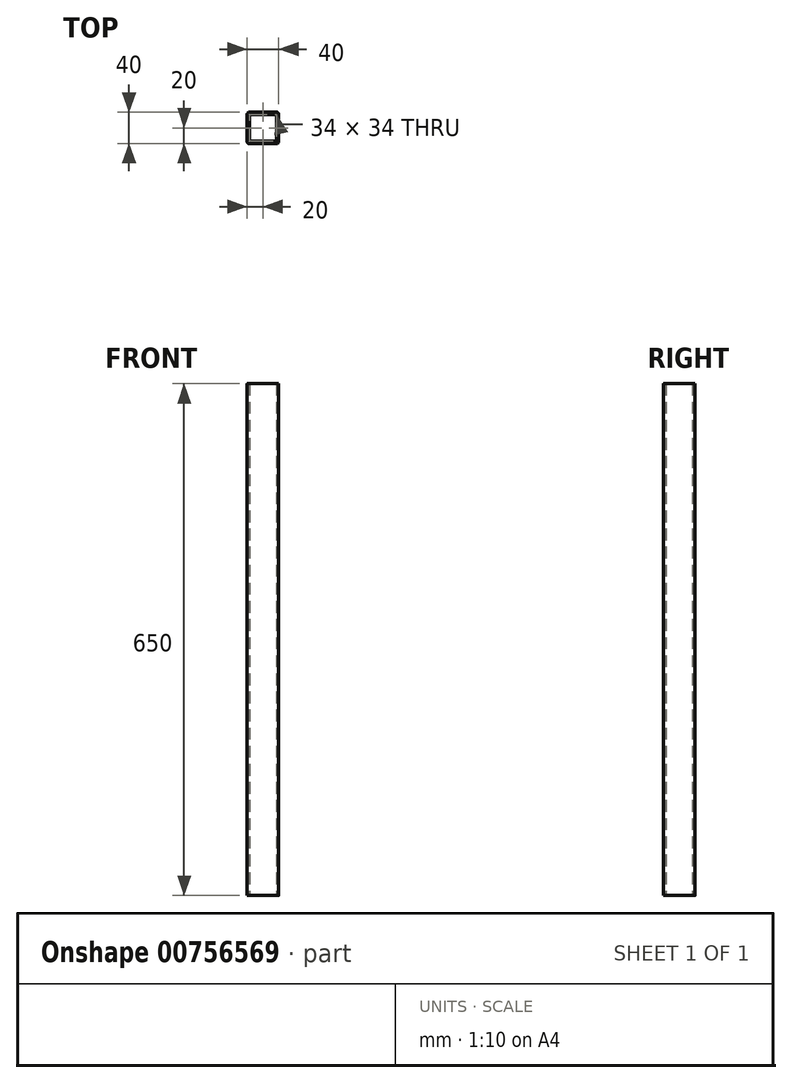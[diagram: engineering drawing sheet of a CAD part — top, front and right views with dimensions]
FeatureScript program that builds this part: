
annotation { "Feature Type Name" : "Feature", "Feature Type Description" : "" }
export const myFeature = defineFeature(function(context is Context, id is Id, definition is map)
    precondition{}
    {
        {
            var Q0;
            Q0=qCreatedBy(makeId("Top.planeOp"),FACE);
            var sketch = newSketch(context, id + "F0", { "sketchPlane" : qUnion([Q0])});
            skLineSegment(sketch, "E0.bottom", {"start": v(2.5, 0) * mm, "end": v(37.5, 0) * mm});
            skLineSegment(sketch, "E0.top", {"start": v(2.5, 40) * mm, "end": v(37.5, 40) * mm});
            skLineSegment(sketch, "E0.left", {"start": v(0, 2.5) * mm, "end": v(0, 37.5) * mm});
            skLineSegment(sketch, "E0.right", {"start": v(40, 2.5) * mm, "end": v(40, 37.5) * mm});
            skLineSegment(sketch, "E1.bottom", {"start": v(3, 3) * mm, "end": v(37, 3) * mm});
            skLineSegment(sketch, "E1.top", {"start": v(3, 37) * mm, "end": v(37, 37) * mm});
            skLineSegment(sketch, "E1.left", {"start": v(3, 3) * mm, "end": v(3, 37) * mm});
            skLineSegment(sketch, "E1.right", {"start": v(37, 3) * mm, "end": v(37, 37) * mm});
            skPoint(sketch, "E2.visualSharp", {"position": v(0, 0) * mm});
            skArc(sketch, "E2.filletArc", {"start": v(0, 2.5) * mm, "mid": v(0.73, 0.73) * mm, "end": v(2.5, 0) * mm});
            skPoint(sketch, "E3.visualSharp", {"position": v(40, 0) * mm});
            skArc(sketch, "E3.filletArc", {"start": v(37.5, 0) * mm, "mid": v(39.27, 0.73) * mm, "end": v(40, 2.5) * mm});
            skPoint(sketch, "E4.visualSharp", {"position": v(40, 40) * mm});
            skArc(sketch, "E4.filletArc", {"start": v(40, 37.5) * mm, "mid": v(39.27, 39.27) * mm, "end": v(37.5, 40) * mm});
            skPoint(sketch, "E5.visualSharp", {"position": v(0, 40) * mm});
            skArc(sketch, "E5.filletArc", {"start": v(2.5, 40) * mm, "mid": v(0.73, 39.27) * mm, "end": v(0, 37.5) * mm});
            skSolve(sketch);
        }
        {
            var Q0;
            Q0 = qSketchRegion(id + "F0", true);
            extrude(context, id + "F1", {"entities" : qUnion([Q0]), "depth" : 650 * mm, "offsetDistance" : 25 * mm});
        }
    });
